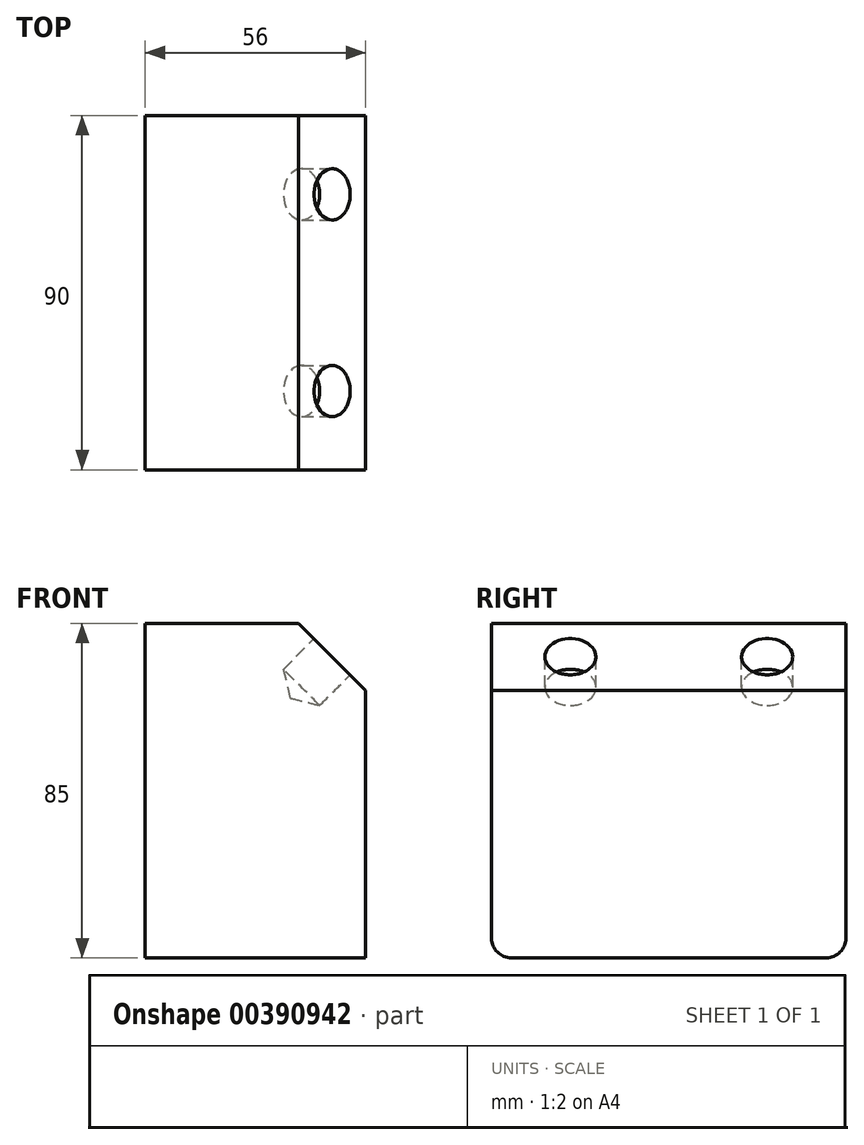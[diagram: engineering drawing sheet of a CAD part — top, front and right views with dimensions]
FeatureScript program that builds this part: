
annotation { "Feature Type Name" : "Feature", "Feature Type Description" : "" }
export const myFeature = defineFeature(function(context is Context, id is Id, definition is map)
    precondition{}
    {
        {
            var Q0;
            Q0=qCreatedBy(makeId("Top.planeOp"),FACE);
            var sketch = newSketch(context, id + "F0", { "sketchPlane" : qUnion([Q0])});
            skLineSegment(sketch, "E0.bottom", {"start": v(0, 0) * mm, "end": v(56, 0) * mm});
            skLineSegment(sketch, "E0.top", {"start": v(0, 90) * mm, "end": v(56, 90) * mm});
            skLineSegment(sketch, "E0.left", {"start": v(0, 0) * mm, "end": v(0, 90) * mm});
            skLineSegment(sketch, "E0.right", {"start": v(56, 0) * mm, "end": v(56, 90) * mm});
            skSolve(sketch);
        }
        {
            var Q0;
            Q0=makeQuery(id+"F0.imprint","IMPRINT",FACE,{"disambiguationData":[TD([[makeQuery(id+"F0.imprint","IMPRINT",EDGE,{"derivedFrom":sQuery(id+"F0.wireOp",EDGE,"E0.bottom")}),1.0]])]});
            extrude(context, id + "F1", {"entities" : qUnion([Q0]), "depth" : 25 * mm});
        }
        {
            var Q0;
            Q0=makeQuery(id+"F1.opExtrude","CAP_FACE",FACE,{"disambiguationData":[OSD([sQuery(id+"F0.wireOp",EDGE,"E0.bottom"),sQuery(id+"F0.wireOp",EDGE,"E0.top"),sQuery(id+"F0.wireOp",EDGE,"E0.left"),sQuery(id+"F0.wireOp",EDGE,"E0.right")])],"isStart":false});
            extrude(context, id + "F2", {"entities" : qUnion([Q0]), "operationType" : NewBodyOperationType.ADD, "depth" : 60 * mm});
        }
        {
            var Q0;
            Q0=makeQuery(id+"F2.opExtrude","CAP_EDGE",EDGE,{"disambiguationData":[OSD([sQuery(id+"F0.wireOp",EDGE,"E0.right")])],"isStart":false});
            chamfer(context, id + "F3", {"entities" : qUnion([Q0]), "width" : 17 * mm, "tangentPropagation" : true});
        }
        {
            var Q0;
            Q0=makeQuery(id+"F3.opChamfer","BLEND_FACE",FACE,{"disambiguationData":[OSD([sQuery(id+"F0.wireOp",EDGE,"E0.right")])]});
            var sketch = newSketch(context, id + "F4", { "sketchPlane" : qUnion([Q0])});
            skCircle(sketch, "E1", {"center": v(20, 20.53) * mm, "radius": 6.7 * mm});
            skCircle(sketch, "E2", {"center": v(70, 20.53) * mm, "radius": 7.35 * mm});
            skSolve(sketch);
        }
        {
            var Q0;
            Q0=sQuery(id+"F4.wireOp",VERTEX,"E1.center");
            var Q1;
            Q1=sQuery(id+"F4.wireOp",VERTEX,"E2.center");
            var Q2;
            Q2=makeQuery(id+"F1.opExtrude","SWEPT_BODY",BODY,{"disambiguationData":[OSD([sQuery(id+"F0.wireOp",EDGE,"E0.bottom"),sQuery(id+"F0.wireOp",EDGE,"E0.top"),sQuery(id+"F0.wireOp",EDGE,"E0.left"),sQuery(id+"F0.wireOp",EDGE,"E0.right")])]});
            hole(context, id + "F5", {"style" : HoleStyle.SIMPLE, "endStyle" : HoleEndStyle.BLIND, "holeDiameter" : 13 * mm, "holeDepth" : 11 * mm, "isTappedThrough" : true, "tappedDepth" : 12 * mm, "tapClearance" : 3, "locations" : qUnion([Q0, Q1]), "scope" : qUnion([Q2])});
        }
        {
            var Q0;
            Q0=makeQuery(id+"F1.opExtrude","CAP_EDGE",EDGE,{"disambiguationData":[OSD([sQuery(id+"F0.wireOp",EDGE,"E0.bottom")])],"isStart":true});
            var Q1;
            Q1=makeQuery(id+"F1.opExtrude","CAP_EDGE",EDGE,{"disambiguationData":[OSD([sQuery(id+"F0.wireOp",EDGE,"E0.top")])],"isStart":true});
            fillet(context, id + "F6", {"entities" : qUnion([Q0, Q1]), "radius" : 5 * mm, "tangentPropagation" : true, "allowEdgeOverflow" : false});
        }
    });
